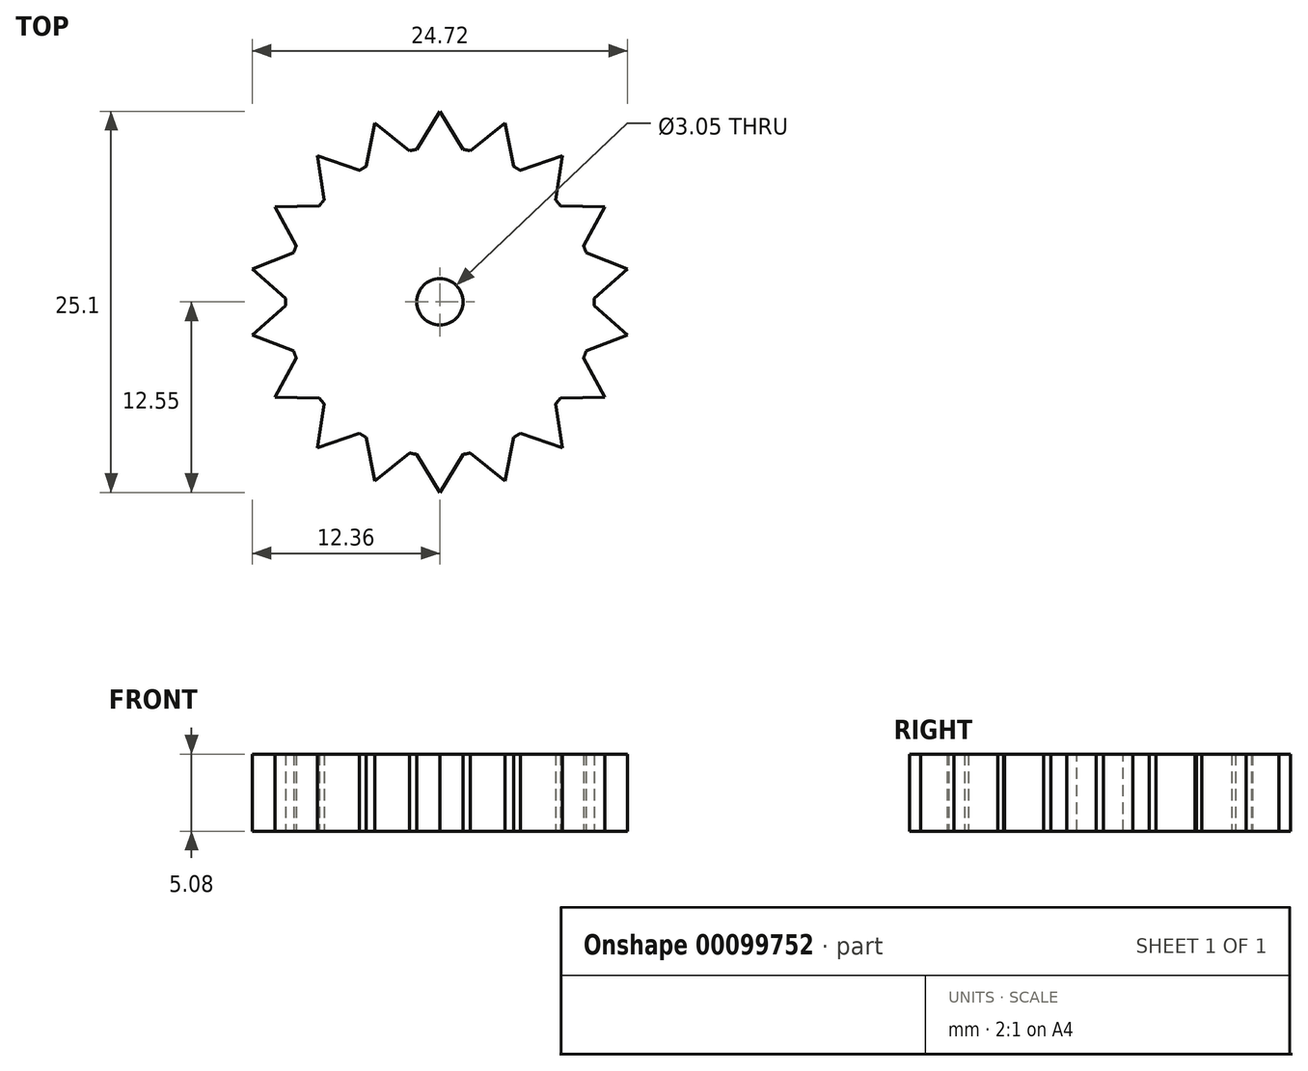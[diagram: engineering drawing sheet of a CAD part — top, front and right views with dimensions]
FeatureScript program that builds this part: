
annotation { "Feature Type Name" : "Feature", "Feature Type Description" : "" }
export const myFeature = defineFeature(function(context is Context, id is Id, definition is map)
    precondition{}
    {
        {
            var Q0;
            Q0=qCreatedBy(makeId("Top.planeOp"),FACE);
            var sketch = newSketch(context, id + "F0", { "sketchPlane" : qUnion([Q0])});
            skCircle(sketch, "E0", {"center": v(0, 0) * mm, "radius": 10.16 * mm});
            skLineSegment(sketch, "E1", {"start": v(-1.52, 10.05) * mm, "end": v(0, 12.55) * mm});
            skLineSegment(sketch, "E2", {"start": v(0, 12.55) * mm, "end": v(1.52, 10.05) * mm});
            skLineSegment(sketch, "E3.1.0", {"start": v(-4.3, 11.8) * mm, "end": v(-2, 9.96) * mm});
            skLineSegment(sketch, "E3.1.1", {"start": v(-4.87, 8.92) * mm, "end": v(-4.3, 11.8) * mm});
            skLineSegment(sketch, "E3.2.0", {"start": v(-8.07, 9.61) * mm, "end": v(-5.29, 8.67) * mm});
            skLineSegment(sketch, "E3.2.1", {"start": v(-7.62, 6.72) * mm, "end": v(-8.07, 9.61) * mm});
            skLineSegment(sketch, "E4.2.3.0", {"start": v(-10.87, 6.28) * mm, "end": v(-7.94, 6.34) * mm});
            skLineSegment(sketch, "E4.3.3.0", {"start": v(-9.46, 3.7) * mm, "end": v(-10.87, 6.28) * mm});
            skLineSegment(sketch, "E4.2.4.0", {"start": v(-12.36, 2.18) * mm, "end": v(-9.63, 3.25) * mm});
            skLineSegment(sketch, "E4.3.4.0", {"start": v(-10.16, 0.24) * mm, "end": v(-12.36, 2.18) * mm});
            skLineSegment(sketch, "E4.2.5.0", {"start": v(-12.36, -2.18) * mm, "end": v(-10.16, -0.24) * mm});
            skLineSegment(sketch, "E4.3.5.0", {"start": v(-9.63, -3.25) * mm, "end": v(-12.36, -2.18) * mm});
            skLineSegment(sketch, "E4.2.6.0", {"start": v(-10.87, -6.28) * mm, "end": v(-9.46, -3.7) * mm});
            skLineSegment(sketch, "E4.3.6.0", {"start": v(-7.94, -6.34) * mm, "end": v(-10.87, -6.28) * mm});
            skLineSegment(sketch, "E4.2.7.0", {"start": v(-8.07, -9.61) * mm, "end": v(-7.62, -6.72) * mm});
            skLineSegment(sketch, "E4.3.7.0", {"start": v(-5.29, -8.67) * mm, "end": v(-8.07, -9.61) * mm});
            skLineSegment(sketch, "E4.2.8.0", {"start": v(-4.3, -11.8) * mm, "end": v(-4.87, -8.92) * mm});
            skLineSegment(sketch, "E4.3.8.0", {"start": v(-2, -9.96) * mm, "end": v(-4.3, -11.8) * mm});
            skLineSegment(sketch, "E4.2.9.0", {"start": v(0, -12.55) * mm, "end": v(-1.52, -10.05) * mm});
            skLineSegment(sketch, "E4.3.9.0", {"start": v(1.52, -10.05) * mm, "end": v(0, -12.55) * mm});
            skLineSegment(sketch, "E5.2.10.0", {"start": v(4.3, -11.8) * mm, "end": v(2, -9.96) * mm});
            skLineSegment(sketch, "E5.3.10.0", {"start": v(4.87, -8.92) * mm, "end": v(4.3, -11.8) * mm});
            skLineSegment(sketch, "E6.2.11.0", {"start": v(8.07, -9.61) * mm, "end": v(5.29, -8.67) * mm});
            skLineSegment(sketch, "E6.3.11.0", {"start": v(7.62, -6.72) * mm, "end": v(8.07, -9.61) * mm});
            skLineSegment(sketch, "E7.2.12.0", {"start": v(10.87, -6.28) * mm, "end": v(7.94, -6.34) * mm});
            skLineSegment(sketch, "E7.3.12.0", {"start": v(9.46, -3.7) * mm, "end": v(10.87, -6.28) * mm});
            skLineSegment(sketch, "E8.2.13.0", {"start": v(12.36, -2.18) * mm, "end": v(9.63, -3.25) * mm});
            skLineSegment(sketch, "E8.3.13.0", {"start": v(10.16, -0.24) * mm, "end": v(12.36, -2.18) * mm});
            skLineSegment(sketch, "E8.2.14.0", {"start": v(12.36, 2.18) * mm, "end": v(10.16, 0.24) * mm});
            skLineSegment(sketch, "E8.3.14.0", {"start": v(9.63, 3.25) * mm, "end": v(12.36, 2.18) * mm});
            skLineSegment(sketch, "E9.2.15.0", {"start": v(10.87, 6.28) * mm, "end": v(9.46, 3.7) * mm});
            skLineSegment(sketch, "E9.3.15.0", {"start": v(7.94, 6.34) * mm, "end": v(10.87, 6.28) * mm});
            skLineSegment(sketch, "E10.2.16.0", {"start": v(8.07, 9.61) * mm, "end": v(7.62, 6.72) * mm});
            skLineSegment(sketch, "E10.3.16.0", {"start": v(5.29, 8.67) * mm, "end": v(8.07, 9.61) * mm});
            skLineSegment(sketch, "E10.2.17.0", {"start": v(4.3, 11.8) * mm, "end": v(4.87, 8.92) * mm});
            skLineSegment(sketch, "E10.3.17.0", {"start": v(2, 9.96) * mm, "end": v(4.3, 11.8) * mm});
            skSolve(sketch);
        }
        {
            var Q0;
            {var subQ0=sQuery(id+"F0.wireOp",EDGE,"E0");var subQ21=makeQuery(id+"F0.imprint","INTERSECT",VERTEX,{"derivedFrom":[subQ0,sQuery(id+"F0.wireOp",EDGE,"E8.2.14.0")]});Q0=makeQuery(id+"F0.imprint","IMPRINT",FACE,{"disambiguationData":[TD([[makeQuery(id+"F0.imprint","IMPRINT",EDGE,{"disambiguationData":[TD([[subQ21,-1.0]])],"derivedFrom":subQ0}),1.0]])]});}
            var Q1;
            {var subQ0=sQuery(id+"F0.wireOp",EDGE,"E6.2.11.0");Q1=makeQuery(id+"F0.imprint","IMPRINT",FACE,{"disambiguationData":[TD([[makeQuery(id+"F0.imprint","IMPRINT",EDGE,{"derivedFrom":subQ0}),-1.0]])]});}
            var Q2;
            {var subQ0=sQuery(id+"F0.wireOp",EDGE,"E4.2.9.0");Q2=makeQuery(id+"F0.imprint","IMPRINT",FACE,{"disambiguationData":[TD([[makeQuery(id+"F0.imprint","IMPRINT",EDGE,{"derivedFrom":subQ0}),-1.0]])]});}
            var Q3;
            {var subQ0=sQuery(id+"F0.wireOp",EDGE,"E5.2.10.0");Q3=makeQuery(id+"F0.imprint","IMPRINT",FACE,{"disambiguationData":[TD([[makeQuery(id+"F0.imprint","IMPRINT",EDGE,{"derivedFrom":subQ0}),-1.0]])]});}
            var Q4;
            {var subQ0=sQuery(id+"F0.wireOp",EDGE,"E8.2.14.0");Q4=makeQuery(id+"F0.imprint","IMPRINT",FACE,{"disambiguationData":[TD([[makeQuery(id+"F0.imprint","IMPRINT",EDGE,{"derivedFrom":subQ0}),-1.0]])]});}
            var Q5;
            {var subQ0=sQuery(id+"F0.wireOp",EDGE,"E9.2.15.0");Q5=makeQuery(id+"F0.imprint","IMPRINT",FACE,{"disambiguationData":[TD([[makeQuery(id+"F0.imprint","IMPRINT",EDGE,{"derivedFrom":subQ0}),-1.0]])]});}
            var Q6;
            {var subQ0=sQuery(id+"F0.wireOp",EDGE,"E10.2.16.0");Q6=makeQuery(id+"F0.imprint","IMPRINT",FACE,{"disambiguationData":[TD([[makeQuery(id+"F0.imprint","IMPRINT",EDGE,{"derivedFrom":subQ0}),-1.0]])]});}
            var Q7;
            {var subQ0=sQuery(id+"F0.wireOp",EDGE,"E10.2.17.0");Q7=makeQuery(id+"F0.imprint","IMPRINT",FACE,{"disambiguationData":[TD([[makeQuery(id+"F0.imprint","IMPRINT",EDGE,{"derivedFrom":subQ0}),-1.0]])]});}
            var Q8;
            {var subQ0=sQuery(id+"F0.wireOp",EDGE,"E1");Q8=makeQuery(id+"F0.imprint","IMPRINT",FACE,{"disambiguationData":[TD([[makeQuery(id+"F0.imprint","IMPRINT",EDGE,{"derivedFrom":subQ0}),-1.0]])]});}
            var Q9;
            {var subQ0=sQuery(id+"F0.wireOp",EDGE,"E7.2.12.0");Q9=makeQuery(id+"F0.imprint","IMPRINT",FACE,{"disambiguationData":[TD([[makeQuery(id+"F0.imprint","IMPRINT",EDGE,{"derivedFrom":subQ0}),-1.0]])]});}
            var Q10;
            {var subQ0=sQuery(id+"F0.wireOp",EDGE,"E3.1.0");Q10=makeQuery(id+"F0.imprint","IMPRINT",FACE,{"disambiguationData":[TD([[makeQuery(id+"F0.imprint","IMPRINT",EDGE,{"derivedFrom":subQ0}),-1.0]])]});}
            var Q11;
            {var subQ0=sQuery(id+"F0.wireOp",EDGE,"E8.2.13.0");Q11=makeQuery(id+"F0.imprint","IMPRINT",FACE,{"disambiguationData":[TD([[makeQuery(id+"F0.imprint","IMPRINT",EDGE,{"derivedFrom":subQ0}),-1.0]])]});}
            var Q12;
            {var subQ0=sQuery(id+"F0.wireOp",EDGE,"E3.2.0");Q12=makeQuery(id+"F0.imprint","IMPRINT",FACE,{"disambiguationData":[TD([[makeQuery(id+"F0.imprint","IMPRINT",EDGE,{"derivedFrom":subQ0}),-1.0]])]});}
            var Q13;
            {var subQ0=sQuery(id+"F0.wireOp",EDGE,"E4.2.3.0");Q13=makeQuery(id+"F0.imprint","IMPRINT",FACE,{"disambiguationData":[TD([[makeQuery(id+"F0.imprint","IMPRINT",EDGE,{"derivedFrom":subQ0}),-1.0]])]});}
            var Q14;
            {var subQ0=sQuery(id+"F0.wireOp",EDGE,"E4.2.4.0");Q14=makeQuery(id+"F0.imprint","IMPRINT",FACE,{"disambiguationData":[TD([[makeQuery(id+"F0.imprint","IMPRINT",EDGE,{"derivedFrom":subQ0}),-1.0]])]});}
            var Q15;
            {var subQ0=sQuery(id+"F0.wireOp",EDGE,"E4.2.6.0");Q15=makeQuery(id+"F0.imprint","IMPRINT",FACE,{"disambiguationData":[TD([[makeQuery(id+"F0.imprint","IMPRINT",EDGE,{"derivedFrom":subQ0}),-1.0]])]});}
            var Q16;
            {var subQ0=sQuery(id+"F0.wireOp",EDGE,"E4.2.5.0");Q16=makeQuery(id+"F0.imprint","IMPRINT",FACE,{"disambiguationData":[TD([[makeQuery(id+"F0.imprint","IMPRINT",EDGE,{"derivedFrom":subQ0}),-1.0]])]});}
            var Q17;
            {var subQ0=sQuery(id+"F0.wireOp",EDGE,"E4.2.7.0");Q17=makeQuery(id+"F0.imprint","IMPRINT",FACE,{"disambiguationData":[TD([[makeQuery(id+"F0.imprint","IMPRINT",EDGE,{"derivedFrom":subQ0}),-1.0]])]});}
            var Q18;
            {var subQ0=sQuery(id+"F0.wireOp",EDGE,"E4.2.8.0");Q18=makeQuery(id+"F0.imprint","IMPRINT",FACE,{"disambiguationData":[TD([[makeQuery(id+"F0.imprint","IMPRINT",EDGE,{"derivedFrom":subQ0}),-1.0]])]});}
            extrude(context, id + "F1", {"entities" : qUnion([Q0, Q1, Q2, Q3, Q4, Q5, Q6, Q7, Q8, Q9, Q10, Q11, Q12, Q13, Q14, Q15, Q16, Q17, Q18]), "depth" : 5.08 * mm});
        }
        {
            var Q0;
            Q0=makeQuery(id+"F1.opExtrude","CAP_FACE",FACE,{"disambiguationData":[OSD([sQuery(id+"F0.wireOp",EDGE,"E0"),sQuery(id+"F0.wireOp",EDGE,"E1"),sQuery(id+"F0.wireOp",EDGE,"E2"),sQuery(id+"F0.wireOp",EDGE,"E3.1.0"),sQuery(id+"F0.wireOp",EDGE,"E3.1.1"),sQuery(id+"F0.wireOp",EDGE,"E3.2.0"),sQuery(id+"F0.wireOp",EDGE,"E3.2.1"),sQuery(id+"F0.wireOp",EDGE,"E4.2.3.0"),sQuery(id+"F0.wireOp",EDGE,"E4.3.3.0"),sQuery(id+"F0.wireOp",EDGE,"E4.2.4.0"),sQuery(id+"F0.wireOp",EDGE,"E4.3.4.0"),sQuery(id+"F0.wireOp",EDGE,"E4.2.5.0"),sQuery(id+"F0.wireOp",EDGE,"E4.3.5.0"),sQuery(id+"F0.wireOp",EDGE,"E4.2.6.0"),sQuery(id+"F0.wireOp",EDGE,"E4.3.6.0"),sQuery(id+"F0.wireOp",EDGE,"E4.2.7.0"),sQuery(id+"F0.wireOp",EDGE,"E4.3.7.0"),sQuery(id+"F0.wireOp",EDGE,"E4.2.8.0"),sQuery(id+"F0.wireOp",EDGE,"E4.3.8.0"),sQuery(id+"F0.wireOp",EDGE,"E4.2.9.0"),sQuery(id+"F0.wireOp",EDGE,"E4.3.9.0"),sQuery(id+"F0.wireOp",EDGE,"E5.2.10.0"),sQuery(id+"F0.wireOp",EDGE,"E5.3.10.0"),sQuery(id+"F0.wireOp",EDGE,"E6.2.11.0"),sQuery(id+"F0.wireOp",EDGE,"E6.3.11.0"),sQuery(id+"F0.wireOp",EDGE,"E7.2.12.0"),sQuery(id+"F0.wireOp",EDGE,"E7.3.12.0"),sQuery(id+"F0.wireOp",EDGE,"E8.2.13.0"),sQuery(id+"F0.wireOp",EDGE,"E8.3.13.0"),sQuery(id+"F0.wireOp",EDGE,"E8.2.14.0"),sQuery(id+"F0.wireOp",EDGE,"E8.3.14.0"),sQuery(id+"F0.wireOp",EDGE,"E9.2.15.0"),sQuery(id+"F0.wireOp",EDGE,"E9.3.15.0"),sQuery(id+"F0.wireOp",EDGE,"E10.2.16.0"),sQuery(id+"F0.wireOp",EDGE,"E10.3.16.0"),sQuery(id+"F0.wireOp",EDGE,"E10.2.17.0"),sQuery(id+"F0.wireOp",EDGE,"E10.3.17.0")])],"isStart":false});
            var sketch = newSketch(context, id + "F2", { "sketchPlane" : qUnion([Q0])});
            skCircle(sketch, "E11", {"center": v(0, 0) * mm, "radius": 1.52 * mm});
            skSolve(sketch);
        }
        {
            var Q0;
            Q0=makeQuery(id+"F2.imprint","IMPRINT",FACE,{"disambiguationData":[TD([[makeQuery(id+"F2.imprint","IMPRINT",EDGE,{"derivedFrom":sQuery(id+"F2.wireOp",EDGE,"E11")}),1.0]])]});
            extrude(context, id + "F3", {"entities" : qUnion([Q0]), "operationType" : NewBodyOperationType.REMOVE, "oppositeDirection" : true, "depth" : 5.08 * mm});
        }
    });
